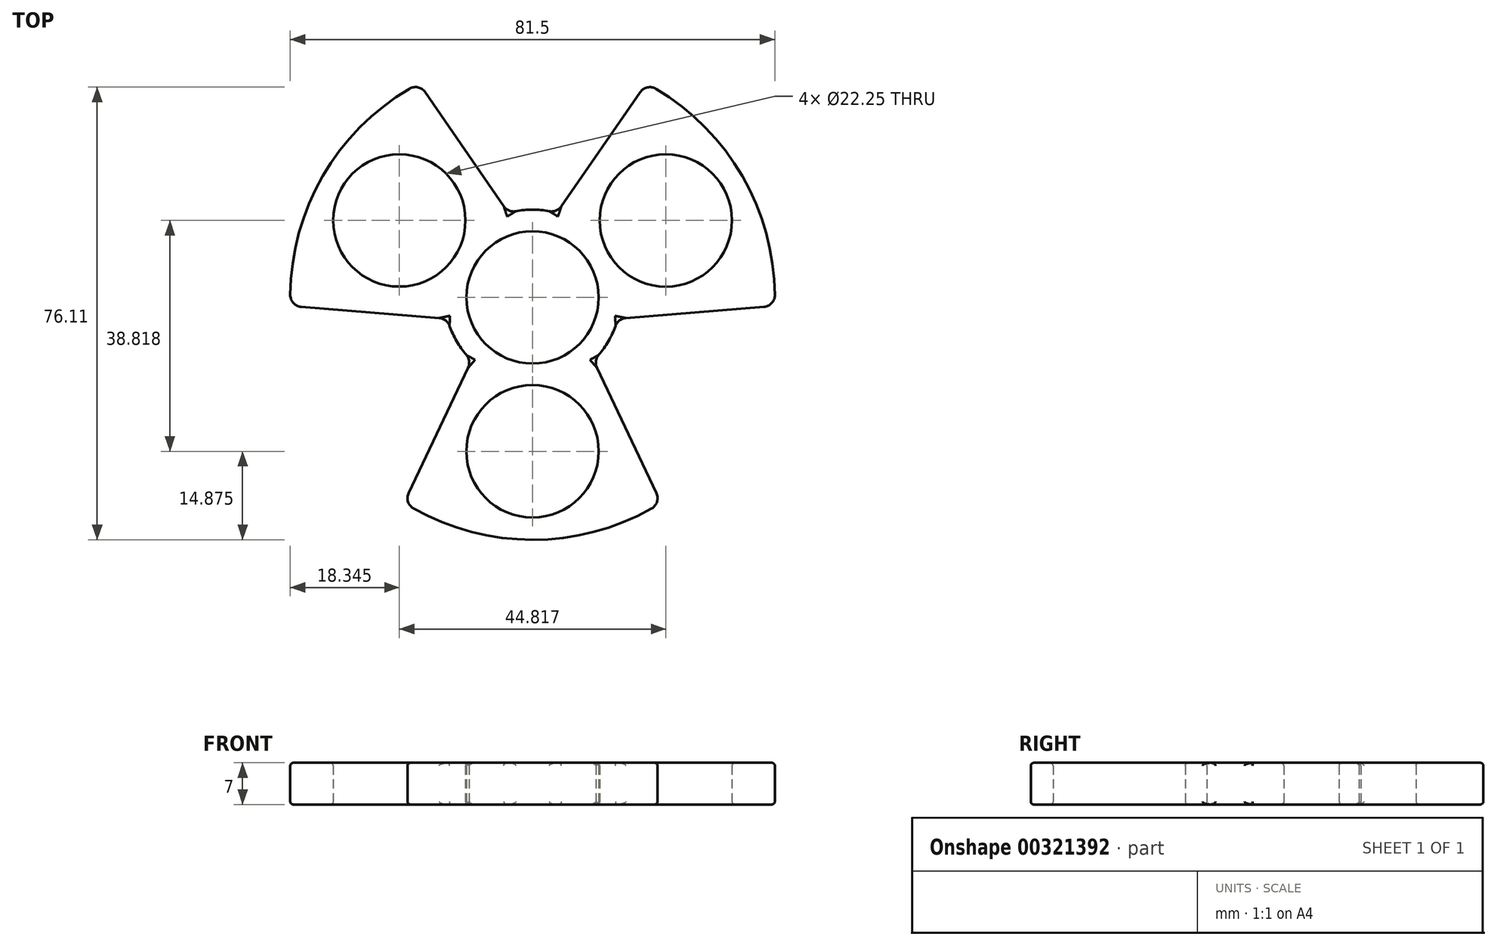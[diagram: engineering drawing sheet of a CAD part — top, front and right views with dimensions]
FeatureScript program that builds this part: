
annotation { "Feature Type Name" : "Feature", "Feature Type Description" : "" }
export const myFeature = defineFeature(function(context is Context, id is Id, definition is map)
    precondition{}
    {
        {
            var Q0;
            Q0=qCreatedBy(makeId("Top.planeOp"),FACE);
            var sketch = newSketch(context, id + "F0", { "sketchPlane" : qUnion([Q0])});
            skCircle(sketch, "E0", {"center": v(0, 0) * mm, "radius": 11.12 * mm});
            skCircle(sketch, "E1", {"center": v(0, 0) * mm, "radius": 14.75 * mm});
            skPoint(sketch, "E2", {"position": v(10.25, -10.6) * mm});
            skPoint(sketch, "E3", {"position": v(-10.25, -10.6) * mm});
            skPoint(sketch, "E4", {"position": v(-21.63, -34.54) * mm});
            skPoint(sketch, "E5", {"position": v(21.6, -34.55) * mm});
            skLineSegment(sketch, "E6", {"start": v(-10.25, -10.6) * mm, "end": v(-21.63, -34.54) * mm});
            skLineSegment(sketch, "E7", {"start": v(10.25, -10.6) * mm, "end": v(21.6, -34.55) * mm});
            skArc(sketch, "E8", {"start": v(21.6, -34.55) * mm, "mid": v(-0.01, -40.75) * mm, "end": v(-21.63, -34.54) * mm});
            skPoint(sketch, "E9", {"position": v(0, -10.6) * mm});
            skPoint(sketch, "E10", {"position": v(0, -11.12) * mm});
            skPoint(sketch, "E11", {"position": v(0, -14.75) * mm});
            skPoint(sketch, "E12.endSnap0", {"position": v(-0.01, -40.75) * mm});
            skPoint(sketch, "E13", {"position": v(0, -37) * mm});
            skPoint(sketch, "E14", {"position": v(0, -25.87) * mm});
            skCircle(sketch, "E15", {"center": v(0, -25.87) * mm, "radius": 11.13 * mm});
            skArc(sketch, "E16.1.0", {"start": v(19.12, 35.99) * mm, "mid": v(35.3, 20.37) * mm, "end": v(40.72, -1.46) * mm});
            skLineSegment(sketch, "E16.1.1", {"start": v(4.06, 14.18) * mm, "end": v(19.12, 35.99) * mm});
            skLineSegment(sketch, "E16.1.2", {"start": v(14.31, -3.57) * mm, "end": v(40.72, -1.46) * mm});
            skCircle(sketch, "E16.1.3", {"center": v(22.41, 12.93) * mm, "radius": 11.13 * mm});
            skArc(sketch, "E16.2.0", {"start": v(-40.72, -1.44) * mm, "mid": v(-35.29, 20.38) * mm, "end": v(-19.1, 36) * mm});
            skLineSegment(sketch, "E16.2.1", {"start": v(-14.31, -3.57) * mm, "end": v(-40.72, -1.44) * mm});
            skLineSegment(sketch, "E16.2.2", {"start": v(-4.06, 14.18) * mm, "end": v(-19.1, 36) * mm});
            skCircle(sketch, "E16.2.3", {"center": v(-22.4, 12.94) * mm, "radius": 11.13 * mm});
            skSolve(sketch);
        }
        {
            var Q0;
            Q0 = qSketchRegion(id + "F0", true);
            extrude(context, id + "F1", {"entities" : qUnion([Q0]), "depth" : 7 * mm});
        }
        {
            var Q0;
            Q0=makeQuery(id+"F1.opExtrude","SWEPT_EDGE",EDGE,{"disambiguationData":[OSD([sQuery(id+"F0.wireOp",EDGE,"E7"),sQuery(id+"F0.wireOp",EDGE,"E8")])]});
            var Q1;
            Q1=makeQuery(id+"F1.opExtrude","SWEPT_EDGE",EDGE,{"disambiguationData":[OSD([sQuery(id+"F0.wireOp",EDGE,"E6"),sQuery(id+"F0.wireOp",EDGE,"E8")])]});
            var Q2;
            Q2=makeQuery(id+"F1.opExtrude","SWEPT_EDGE",EDGE,{"disambiguationData":[OSD([sQuery(id+"F0.wireOp",EDGE,"E16.2.0"),sQuery(id+"F0.wireOp",EDGE,"E16.2.1")])]});
            var Q3;
            Q3=makeQuery(id+"F1.opExtrude","SWEPT_EDGE",EDGE,{"disambiguationData":[OSD([sQuery(id+"F0.wireOp",EDGE,"E16.2.0"),sQuery(id+"F0.wireOp",EDGE,"E16.2.2")])]});
            var Q4;
            Q4=makeQuery(id+"F1.opExtrude","SWEPT_EDGE",EDGE,{"disambiguationData":[OSD([sQuery(id+"F0.wireOp",EDGE,"E16.1.0"),sQuery(id+"F0.wireOp",EDGE,"E16.1.1")])]});
            var Q5;
            Q5=makeQuery(id+"F1.opExtrude","SWEPT_EDGE",EDGE,{"disambiguationData":[OSD([sQuery(id+"F0.wireOp",EDGE,"E16.1.0"),sQuery(id+"F0.wireOp",EDGE,"E16.1.2")])]});
            fillet(context, id + "F2", {"entities" : qUnion([Q0, Q1, Q2, Q3, Q4, Q5]), "radius" : 2 * mm, "tangentPropagation" : true, "allowEdgeOverflow" : false});
        }
        {
            var Q0;
            Q0=makeQuery(id+"F1.opExtrude","CAP_FACE",FACE,{"disambiguationData":[OSD([sQuery(id+"F0.wireOp",EDGE,"E0"),sQuery(id+"F0.wireOp",EDGE,"E1"),sQuery(id+"F0.wireOp",EDGE,"E6"),sQuery(id+"F0.wireOp",EDGE,"E7"),sQuery(id+"F0.wireOp",EDGE,"E8"),sQuery(id+"F0.wireOp",EDGE,"E15"),sQuery(id+"F0.wireOp",EDGE,"E16.1.0"),sQuery(id+"F0.wireOp",EDGE,"E16.1.1"),sQuery(id+"F0.wireOp",EDGE,"E16.1.2"),sQuery(id+"F0.wireOp",EDGE,"E16.1.3"),sQuery(id+"F0.wireOp",EDGE,"E16.2.0"),sQuery(id+"F0.wireOp",EDGE,"E16.2.1"),sQuery(id+"F0.wireOp",EDGE,"E16.2.2"),sQuery(id+"F0.wireOp",EDGE,"E16.2.3")])],"isStart":true});
            var Q1;
            Q1=makeQuery(id+"F1.opExtrude","CAP_FACE",FACE,{"disambiguationData":[OSD([sQuery(id+"F0.wireOp",EDGE,"E0"),sQuery(id+"F0.wireOp",EDGE,"E1"),sQuery(id+"F0.wireOp",EDGE,"E6"),sQuery(id+"F0.wireOp",EDGE,"E7"),sQuery(id+"F0.wireOp",EDGE,"E8"),sQuery(id+"F0.wireOp",EDGE,"E15"),sQuery(id+"F0.wireOp",EDGE,"E16.1.0"),sQuery(id+"F0.wireOp",EDGE,"E16.1.1"),sQuery(id+"F0.wireOp",EDGE,"E16.1.2"),sQuery(id+"F0.wireOp",EDGE,"E16.1.3"),sQuery(id+"F0.wireOp",EDGE,"E16.2.0"),sQuery(id+"F0.wireOp",EDGE,"E16.2.1"),sQuery(id+"F0.wireOp",EDGE,"E16.2.2"),sQuery(id+"F0.wireOp",EDGE,"E16.2.3")])],"isStart":false});
            fillet(context, id + "F3", {"entities" : qUnion([Q0, Q1]), "radius" : .5 * mm, "tangentPropagation" : true, "allowEdgeOverflow" : false});
        }
        {
            var Q0;
            Q0=makeQuery(id+"F1.opExtrude","SWEPT_EDGE",EDGE,{"disambiguationData":[OSD([sQuery(id+"F0.wireOp",EDGE,"E1"),sQuery(id+"F0.wireOp",EDGE,"E16.2.2")])]});
            var Q1;
            Q1=makeQuery(id+"F1.opExtrude","SWEPT_EDGE",EDGE,{"disambiguationData":[OSD([sQuery(id+"F0.wireOp",EDGE,"E1"),sQuery(id+"F0.wireOp",EDGE,"E16.1.1")])]});
            var Q2;
            Q2=makeQuery(id+"F1.opExtrude","SWEPT_EDGE",EDGE,{"disambiguationData":[OSD([sQuery(id+"F0.wireOp",EDGE,"E1"),sQuery(id+"F0.wireOp",EDGE,"E16.1.2")])]});
            var Q3;
            Q3=makeQuery(id+"F1.opExtrude","SWEPT_EDGE",EDGE,{"disambiguationData":[OSD([sQuery(id+"F0.wireOp",EDGE,"E1"),sQuery(id+"F0.wireOp",EDGE,"E7")])]});
            var Q4;
            Q4=makeQuery(id+"F1.opExtrude","SWEPT_EDGE",EDGE,{"disambiguationData":[OSD([sQuery(id+"F0.wireOp",EDGE,"E1"),sQuery(id+"F0.wireOp",EDGE,"E6")])]});
            var Q5;
            Q5=makeQuery(id+"F1.opExtrude","SWEPT_EDGE",EDGE,{"disambiguationData":[OSD([sQuery(id+"F0.wireOp",EDGE,"E1"),sQuery(id+"F0.wireOp",EDGE,"E16.2.1")])]});
            fillet(context, id + "F4", {"entities" : qUnion([Q0, Q1, Q2, Q3, Q4, Q5]), "radius" : 2 * mm, "tangentPropagation" : true, "allowEdgeOverflow" : false});
        }
    });
